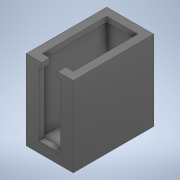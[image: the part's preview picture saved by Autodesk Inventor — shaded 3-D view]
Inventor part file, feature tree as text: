
AUTODESK INVENTOR PART (.ipt)
format: ipt  version: 2020 (Build 240168000, 168)  size: 150,528 bytes
history: native  units: in
note: dims shown in document units (in); Inventor stores cm internally (conversion verified against a paired STEP export)
features: extrude x4, sketch x4, projected_geometry x2
ambient origin geometry x8: Origin, YZ Plane, XZ Plane, XY Plane, X Axis, Y Axis, Z Axis, Center Point
bodies: Solid1 (feature_tree)
feature tree (10):
  extrude  "Extrusion1"  Depth=0.5157in
  extrude  "Extrusion2"  Depth=0.5512in TaperAngle=0.0deg
  extrude  "Extrusion3"  Depth=0.0394in
  extrude  "Extrusion4"  Depth=0.0394in TaperAngle=0.0deg
  sketch  "Sketch1"  dims[d0=0.2677in d1=0.5157in]
  sketch  "Sketch3"  dims[d2=0.0394in d3=0.5512in d4=0.0in]
  projected_geometry  "Projected Loop1"
  sketch  "Sketch4"  dims[d5=0.0394in d6=0.0in d7=0.0394in]
  sketch  "Sketch5"  dims[d8=0.1575in d9=0.0394in d10=0.0in d11=0.0197in d12=0.0394in d13=0.0in]
  projected_geometry  "Projected Loop2"
